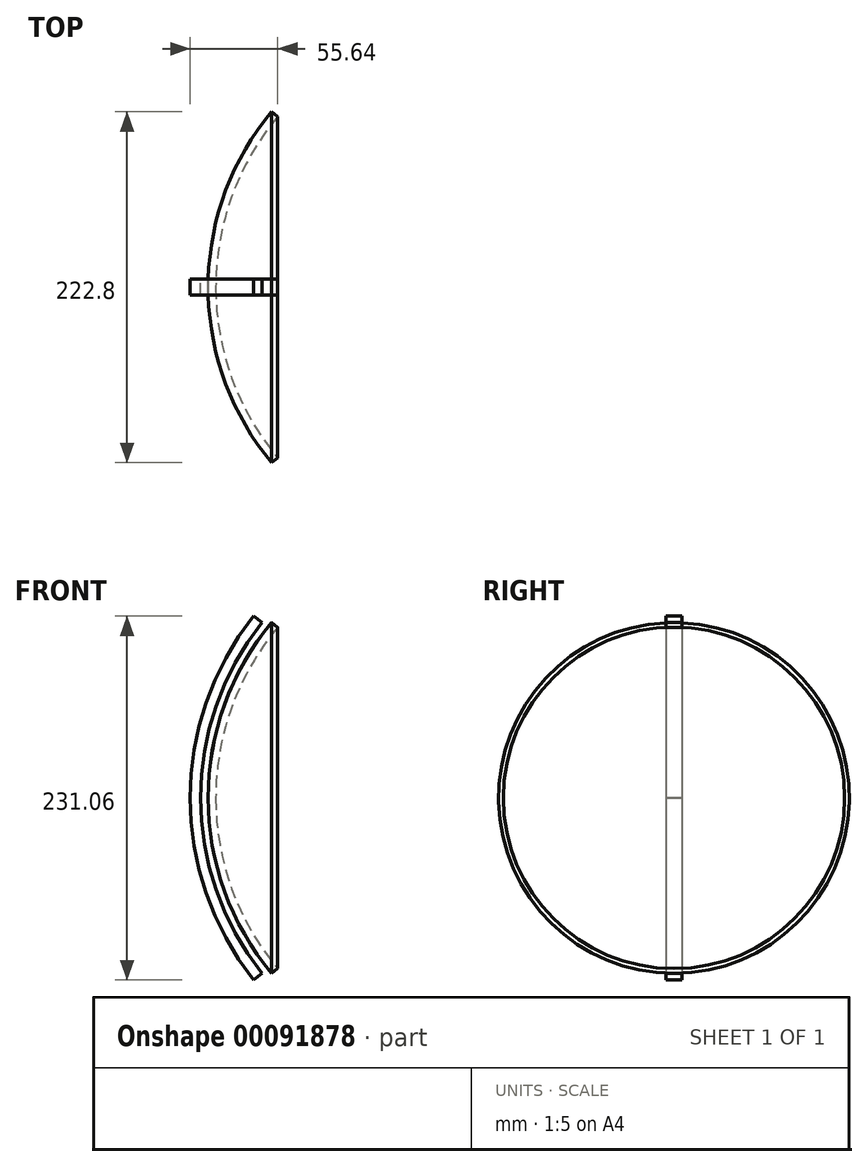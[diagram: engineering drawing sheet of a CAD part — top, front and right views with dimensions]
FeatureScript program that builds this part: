
annotation { "Feature Type Name" : "Feature", "Feature Type Description" : "" }
export const myFeature = defineFeature(function(context is Context, id is Id, definition is map)
    precondition{}
    {
        {
            var Q0;
            Q0=qCreatedBy(makeId("Front.planeOp"),FACE);
            var sketch = newSketch(context, id + "F0", { "sketchPlane" : qUnion([Q0])});
            skArc(sketch, "E0", {"start": v(22.05, 108.4) * mm, "mid": v(-7.13, 57.65) * mm, "end": v(-17.26, 0) * mm});
            skArc(sketch, "E1", {"start": v(18.17, 111.4) * mm, "mid": v(-11.76, 59.24) * mm, "end": v(-22.15, 0) * mm});
            skLineSegment(sketch, "E2", {"start": v(-22.15, 0) * mm, "end": v(-17.26, 0) * mm});
            skLineSegment(sketch, "E3", {"start": v(22.05, 108.4) * mm, "end": v(18.17, 111.4) * mm});
            skLineSegment(sketch, "E4", {"start": v(57.3, 0) * mm, "end": v(87.1, 0) * mm});
            skArc(sketch, "E5", {"start": v(12.1, 111.4) * mm, "mid": v(-26.87, 0) * mm, "end": v(12.1, -111.4) * mm});
            skArc(sketch, "E6", {"start": v(6.78, 115.53) * mm, "mid": v(-33.6, 0) * mm, "end": v(6.78, -115.53) * mm});
            skLineSegment(sketch, "E7", {"start": v(12.1, 111.4) * mm, "end": v(6.78, 115.53) * mm});
            skLineSegment(sketch, "E8", {"start": v(12.1, -111.4) * mm, "end": v(6.78, -115.53) * mm});
            skSolve(sketch);
        }
        {
            var Q0;
            Q0=makeQuery(id+"F0.imprint","IMPRINT",FACE,{"disambiguationData":[TD([[makeQuery(id+"F0.imprint","IMPRINT",EDGE,{"derivedFrom":sQuery(id+"F0.wireOp",EDGE,"E0")}),-1.0]])]});
            var Q1;
            Q1=sQuery(id+"F0.wireOp",EDGE,"E4");
            revolve(context, id + "F1", {"entities" : qUnion([Q0]), "axis" : qUnion([Q1]), "revolveType" : RevolveType.FULL});
        }
        {
            var Q0;
            Q0=makeQuery(id+"F0.imprint","IMPRINT",FACE,{"disambiguationData":[TD([[makeQuery(id+"F0.imprint","IMPRINT",EDGE,{"derivedFrom":sQuery(id+"F0.wireOp",EDGE,"E0")}),-1.0]])]});
            extrude(context, id + "F2", {"entities" : qUnion([Q0]), "operationType" : NewBodyOperationType.ADD, "depth" : 10 * mm, "symmetric" : true});
        }
        {
            var Q0;
            Q0=makeQuery(id+"F0.imprint","IMPRINT",FACE,{"disambiguationData":[TD([[makeQuery(id+"F0.imprint","IMPRINT",EDGE,{"derivedFrom":sQuery(id+"F0.wireOp",EDGE,"E5")}),-1.0]])]});
            extrude(context, id + "F3", {"entities" : qUnion([Q0]), "depth" : 10 * mm, "symmetric" : true});
        }
    });
